# Revit family: Door-Exterior-Simpson-Traditional-Solid_Panel
name_source: partatom
category: Doors
revit_build: Autodesk Revit Architecture 2012 (Build: 20110916_2132(x64)
units: mm (PartAtom-declared; Revit-internal decimal feet)

## types (72) — shared parameters
Assembly Code = B2030230
Default Sill Height = 0"
Description = Traditional - Single Panel
Frame = Wood - Simpson Doors - Douglas Fir
Frame Width = 3"
Function = Exterior
Manufacturer = Simpson Door Company
Panel = Wood - Simpson Doors - Douglas Fir
Product Documentation Link = http://www.simpsondoor.com
Product Page URL = http://www.simpsondoor.com
Thickness = 1 3/4"
URL = http://www.simpsondoor.com
UltraBlock Note = This Door Comes with The Option of UltraBlock Technology. It is Turn On as a Default
UltraBlock Option = Yes
Wall Closure = By host
WaterBarrier Note = This Door Comes with The Option of WaterBarrier with UltraBlock Technology. It is Turn Off as a Default
WaterBarrier with UltraBlock Technology = No
Wood Species = http://simpsondoor.com
Wood Species Note = Available in Any Wood Species

## per-type parameters (varying)
| type | Bottom Rail Height | Height | Model | Panel Stile Width | Panel Thickness | Rough Height | Rough Width | Top Rail Height | Width |
| 20 Traditional 12x80 | 8 13/16" | 80" | 20 | 4 1/8" | 5/8" | 77" | 6" | 4 1/16" | 12" |
| 20 Traditional 12x84 | 10 13/16" | 84" | 20 | 4 1/8" | 5/8" | 81" | 6" | 6 1/16" | 12" |
| 20 Traditional 12x96 | 8 13/16" | 96" | 20 | 4 1/8" | 5/8" | 93" | 6" | 4 1/16" | 12" |
| 20 Traditional 22x80 | 8 13/16" | 80" | 20 | 4 1/8" | 5/8" | 77" | 16" | 4 1/16" | 22" |
| 20 Traditional 22x84 | 10 13/16" | 84" | 20 | 4 1/8" | 5/8" | 81" | 16" | 6 1/16" | 22" |
| 20 Traditional 22x96 | 8 13/16" | 96" | 20 | 4 1/8" | 5/8" | 93" | 16" | 4 1/16" | 22" |
| 20 Traditional 24x80 | 8 13/16" | 80" | 20 | 4 1/8" | 5/8" | 77" | 18" | 4 1/16" | 24" |
| 20 Traditional 24x84 | 10 13/16" | 84" | 20 | 4 1/8" | 5/8" | 81" | 18" | 6 1/16" | 24" |
| 20 Traditional 24x96 | 8 13/16" | 96" | 20 | 4 1/8" | 5/8" | 93" | 18" | 4 1/16" | 24" |
| 20 Traditional 26x80 | 8 13/16" | 80" | 20 | 4 1/8" | 5/8" | 77" | 20" | 4 1/16" | 26" |
| 20 Traditional 26x84 | 10 13/16" | 84" | 20 | 4 1/8" | 5/8" | 81" | 20" | 6 1/16" | 26" |
| 20 Traditional 26x96 | 8 13/16" | 96" | 20 | 4 1/8" | 5/8" | 93" | 20" | 4 1/16" | 26" |
| 20 Traditional 28x80 | 8 13/16" | 80" | 20 | 4 1/8" | 5/8" | 77" | 22" | 4 1/16" | 28" |
| 20 Traditional 28x84 | 10 13/16" | 84" | 20 | 4 1/8" | 5/8" | 81" | 22" | 6 1/16" | 28" |
| 20 Traditional 28x96 | 8 13/16" | 96" | 20 | 4 1/8" | 5/8" | 93" | 22" | 4 1/16" | 28" |
| 20 Traditional 30x80 | 8 13/16" | 80" | 20 | 4 1/8" | 5/8" | 77" | 24" | 4 1/16" | 30" |
| 20 Traditional 30x84 | 10 13/16" | 84" | 20 | 4 1/8" | 5/8" | 81" | 24" | 6 1/16" | 30" |
| 20 Traditional 30x96 | 8 13/16" | 96" | 20 | 4 1/8" | 5/8" | 93" | 24" | 4 1/16" | 30" |
| 20 Traditional 32x80 | 8 13/16" | 80" | 20 | 4 1/8" | 5/8" | 77" | 26" | 4 1/16" | 32" |
| 20 Traditional 32x84 | 10 13/16" | 84" | 20 | 4 1/8" | 5/8" | 81" | 26" | 6 1/16" | 32" |
| 20 Traditional 32x96 | 8 13/16" | 96" | 20 | 4 1/8" | 5/8" | 93" | 26" | 4 1/16" | 32" |
| 20 Traditional 34x80 | 8 13/16" | 80" | 20 | 4 1/8" | 5/8" | 77" | 28" | 4 1/16" | 34" |
| 20 Traditional 34x84 | 10 13/16" | 84" | 20 | 4 1/8" | 5/8" | 81" | 28" | 6 1/16" | 34" |
| 20 Traditional 34x96 | 8 13/16" | 96" | 20 | 4 1/8" | 5/8" | 93" | 28" | 4 1/16" | 34" |
| 20 Traditional 36x80 | 8 13/16" | 80" | 20 | 4 1/8" | 5/8" | 77" | 30" | 4 1/16" | 36" |
| 20 Traditional 36x84 | 10 13/16" | 84" | 20 | 4 1/8" | 5/8" | 81" | 30" | 6 1/16" | 36" |
| 20 Traditional 36x96 | 8 13/16" | 96" | 20 | 4 1/8" | 5/8" | 93" | 30" | 4 1/16" | 36" |
| 20 Traditional 38x80 | 8 13/16" | 80" | 20 | 4 1/8" | 5/8" | 77" | 32" | 4 1/16" | 38" |
| 20 Traditional 38x84 | 10 13/16" | 84" | 20 | 4 1/8" | 5/8" | 81" | 32" | 6 1/16" | 38" |
| 20 Traditional 38x96 | 8 13/16" | 96" | 20 | 4 1/8" | 5/8" | 93" | 32" | 4 1/16" | 38" |
| 20 Traditional 40x80 | 8 13/16" | 80" | 20 | 4 1/8" | 5/8" | 77" | 34" | 4 1/16" | 40" |
| 20 Traditional 40x84 | 10 13/16" | 84" | 20 | 4 1/8" | 5/8" | 81" | 34" | 6 1/16" | 40" |
| 20 Traditional 40x96 | 8 13/16" | 96" | 20 | 4 1/8" | 5/8" | 93" | 34" | 4 1/16" | 40" |
| 20 Traditional 42x80 | 8 13/16" | 80" | 20 | 4 1/8" | 5/8" | 77" | 36" | 4 1/16" | 42" |
| 20 Traditional 42x84 | 10 13/16" | 84" | 20 | 4 1/8" | 5/8" | 81" | 36" | 6 1/16" | 42" |
| 20 Traditional 42x96 | 8 13/16" | 96" | 20 | 4 1/8" | 5/8" | 93" | 36" | 4 1/16" | 42" |
| 7220 Traditional 12x80 | 8 11/16" | 80" | 7220 | 4" | 3/4" | 77" | 6" | 3 15/16" | 12" |
| 7220 Traditional 12x84 | 10 11/16" | 84" | 7220 | 4" | 3/4" | 81" | 6" | 5 15/16" | 12" |
| 7220 Traditional 12x96 | 8 11/16" | 96" | 7220 | 4" | 3/4" | 93" | 6" | 3 15/16" | 12" |
| 7220 Traditional 22x80 | 8 11/16" | 80" | 7220 | 4" | 3/4" | 77" | 16" | 3 15/16" | 22" |
| 7220 Traditional 22x84 | 10 11/16" | 84" | 7220 | 4" | 3/4" | 81" | 16" | 5 15/16" | 22" |
| 7220 Traditional 22x96 | 8 11/16" | 96" | 7220 | 4" | 3/4" | 93" | 16" | 3 15/16" | 22" |
| 7220 Traditional 24x80 | 8 11/16" | 80" | 7220 | 4" | 3/4" | 77" | 18" | 3 15/16" | 24" |
| 7220 Traditional 24x84 | 10 11/16" | 84" | 7220 | 4" | 3/4" | 81" | 18" | 5 15/16" | 24" |
| 7220 Traditional 24x96 | 8 11/16" | 96" | 7220 | 4" | 3/4" | 93" | 18" | 3 15/16" | 24" |
| 7220 Traditional 26x80 | 8 11/16" | 80" | 7220 | 4" | 3/4" | 77" | 20" | 3 15/16" | 26" |
| 7220 Traditional 26x84 | 10 11/16" | 84" | 7220 | 4" | 3/4" | 81" | 20" | 5 15/16" | 26" |
| 7220 Traditional 26x96 | 8 11/16" | 96" | 7220 | 4" | 3/4" | 93" | 20" | 3 15/16" | 26" |
| 7220 Traditional 28x80 | 8 11/16" | 80" | 7220 | 4" | 3/4" | 77" | 22" | 3 15/16" | 28" |
| 7220 Traditional 28x84 | 10 11/16" | 84" | 7220 | 4" | 3/4" | 81" | 22" | 5 15/16" | 28" |
| 7220 Traditional 28x96 | 8 11/16" | 96" | 7220 | 4" | 3/4" | 93" | 22" | 3 15/16" | 28" |
| 7220 Traditional 30x80 | 8 11/16" | 80" | 7220 | 4" | 3/4" | 77" | 24" | 3 15/16" | 30" |
| 7220 Traditional 30x84 | 10 11/16" | 84" | 7220 | 4" | 3/4" | 81" | 24" | 5 15/16" | 30" |
| 7220 Traditional 30x96 | 8 11/16" | 96" | 7220 | 4" | 3/4" | 93" | 24" | 3 15/16" | 30" |
| 7220 Traditional 32x80 | 8 11/16" | 80" | 7220 | 4" | 3/4" | 77" | 26" | 3 15/16" | 32" |
| 7220 Traditional 32x84 | 10 11/16" | 84" | 7220 | 4" | 3/4" | 81" | 26" | 5 15/16" | 32" |
| 7220 Traditional 32x96 | 8 11/16" | 96" | 7220 | 4" | 3/4" | 93" | 26" | 3 15/16" | 32" |
| 7220 Traditional 34x80 | 8 11/16" | 80" | 7220 | 4" | 3/4" | 77" | 28" | 3 15/16" | 34" |
| 7220 Traditional 34x84 | 10 11/16" | 84" | 7220 | 4" | 3/4" | 81" | 28" | 5 15/16" | 34" |
| 7220 Traditional 34x96 | 8 11/16" | 96" | 7220 | 4" | 3/4" | 93" | 28" | 3 15/16" | 34" |
| 7220 Traditional 36x80 | 8 11/16" | 80" | 7220 | 4" | 3/4" | 77" | 30" | 3 15/16" | 36" |
| 7220 Traditional 36x84 | 10 11/16" | 84" | 7220 | 4" | 3/4" | 81" | 30" | 5 15/16" | 36" |
| 7220 Traditional 36x96 | 8 11/16" | 96" | 7220 | 4" | 3/4" | 93" | 30" | 3 15/16" | 36" |
| 7220 Traditional 38x80 | 8 11/16" | 80" | 7220 | 4" | 3/4" | 77" | 32" | 3 15/16" | 38" |
| 7220 Traditional 38x84 | 10 11/16" | 84" | 7220 | 4" | 3/4" | 81" | 32" | 5 15/16" | 38" |
| 7220 Traditional 38x96 | 8 11/16" | 96" | 7220 | 4" | 3/4" | 93" | 32" | 3 15/16" | 38" |
| 7220 Traditional 40x80 | 8 11/16" | 80" | 7220 | 4" | 3/4" | 77" | 34" | 3 15/16" | 40" |
| 7220 Traditional 40x84 | 10 11/16" | 84" | 7220 | 4" | 3/4" | 81" | 34" | 5 15/16" | 40" |
| 7220 Traditional 40x96 | 8 11/16" | 96" | 7220 | 4" | 3/4" | 93" | 34" | 3 15/16" | 40" |
| 7220 Traditional 42x80 | 8 11/16" | 80" | 7220 | 4" | 3/4" | 77" | 36" | 3 15/16" | 42" |
| 7220 Traditional 42x84 | 10 11/16" | 84" | 7220 | 4" | 3/4" | 81" | 36" | 5 15/16" | 42" |
| 7220 Traditional 42x96 | 8 11/16" | 96" | 7220 | 4" | 3/4" | 93" | 36" | 3 15/16" | 42" |

## geometry (parser evidence)
native form markers: Blend x30, Sweep x14
no freeform markers — native parametric forms only
